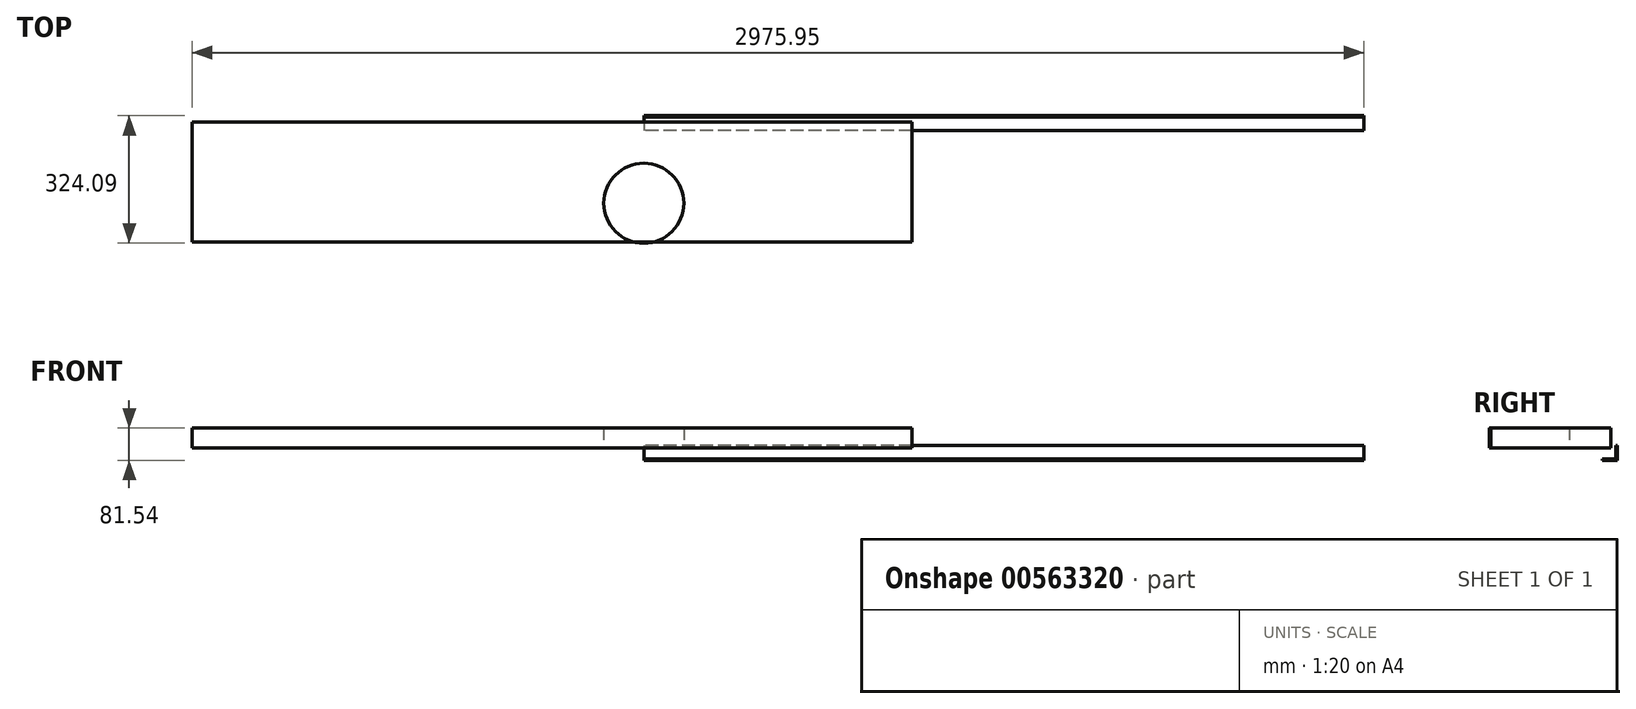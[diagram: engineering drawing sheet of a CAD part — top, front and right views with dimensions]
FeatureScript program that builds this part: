
annotation { "Feature Type Name" : "Feature", "Feature Type Description" : "" }
export const myFeature = defineFeature(function(context is Context, id is Id, definition is map)
    precondition{}
    {
        {
            var Q0;
            Q0=qCreatedBy(makeId("Top.planeOp"),FACE);
            var sketch = newSketch(context, id + "F0", { "sketchPlane" : qUnion([Q0])});
            skCircle(sketch, "E0", {"center": v(0, 0) * mm, "radius": 101.6 * mm});
            skSolve(sketch);
        }
        {
            var Q0;
            Q0 = qSketchRegion(id + "F0", true);
            extrude(context, id + "F1", {"entities" : qUnion([Q0]), "depth" : 50.8 * mm, "offsetDistance" : 25.4 * mm});
        }
        {
            var Q0;
            Q0=qCreatedBy(makeId("Top.planeOp"),FACE);
            var sketch = newSketch(context, id + "F2", { "sketchPlane" : qUnion([Q0])});
            skLineSegment(sketch, "E1.bottom", {"start": v(-1147.15, 206.8) * mm, "end": v(681.65, 206.8) * mm});
            skLineSegment(sketch, "E1.top", {"start": v(-1147.15, -98) * mm, "end": v(681.65, -98) * mm});
            skLineSegment(sketch, "E1.left", {"start": v(-1147.15, 206.8) * mm, "end": v(-1147.15, -98) * mm});
            skLineSegment(sketch, "E1.right", {"start": v(681.65, 206.8) * mm, "end": v(681.65, -98) * mm});
            skSolve(sketch);
        }
        {
            var Q0;
            Q0 = qSketchRegion(id + "F2", true);
            extrude(context, id + "F3", {"entities" : qUnion([Q0]), "depth" : 50.8 * mm, "offsetDistance" : 25.4 * mm});
        }
        {
            var Q0;
            Q0=qCreatedBy(makeId("Right.planeOp"),FACE);
            var sketch = newSketch(context, id + "F4", { "sketchPlane" : qUnion([Q0])});
            skLineSegment(sketch, "E2.bottom", {"start": v(222.49, 7.36) * mm, "end": v(219.31, 7.36) * mm});
            skLineSegment(sketch, "E2.top", {"start": v(222.49, -30.74) * mm, "end": v(219.31, -30.74) * mm});
            skLineSegment(sketch, "E2.left", {"start": v(222.49, 7.36) * mm, "end": v(222.49, -30.74) * mm});
            skLineSegment(sketch, "E2.right", {"start": v(219.31, 7.36) * mm, "end": v(219.31, -30.74) * mm});
            skLineSegment(sketch, "E3.bottom", {"start": v(219.31, -30.74) * mm, "end": v(184.39, -30.74) * mm});
            skLineSegment(sketch, "E3.top", {"start": v(219.31, -27.56) * mm, "end": v(184.39, -27.56) * mm});
            skLineSegment(sketch, "E3.left", {"start": v(219.31, -30.74) * mm, "end": v(219.31, -27.56) * mm});
            skLineSegment(sketch, "E3.right", {"start": v(184.39, -30.74) * mm, "end": v(184.39, -27.56) * mm});
            skSolve(sketch);
        }
        {
            var Q0;
            Q0 = qSketchRegion(id + "F4", true);
            extrude(context, id + "F5", {"entities" : qUnion([Q0]), "depth" : 1828.8 * mm, "offsetDistance" : 25.4 * mm});
        }
    });
